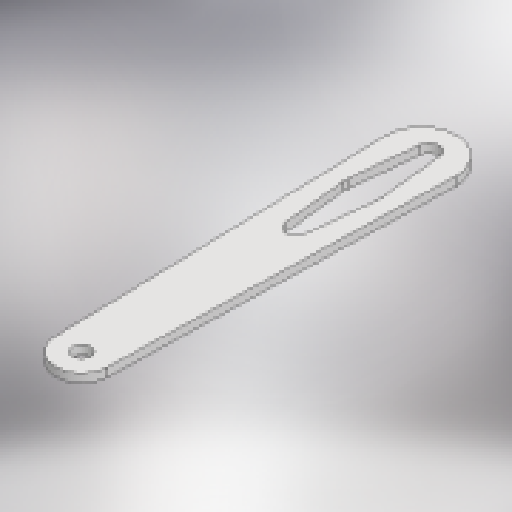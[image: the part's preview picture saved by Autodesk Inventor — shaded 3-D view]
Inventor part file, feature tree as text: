
AUTODESK INVENTOR PART (.ipt)
format: ipt  version: 2024 (Build 280153000, 153)  size: 201,216 bytes
history: native  units: in
note: dims shown in document units (in); Inventor stores cm internally (conversion verified against a paired STEP export)
features: extrude x2, sketch x2, projected_geometry x1
ambient origin geometry x8: Origin, YZ Plane, XZ Plane, XY Plane, X Axis, Y Axis, Z Axis, Center Point
bodies: Solid1 (feature_tree)
feature tree (5):
  extrude  "Extrusion1"  Depth=0.0625in
  extrude  "Extrusion2"  Depth=0.0625in
  sketch  "Sketch1"  dims[d2=0.0625in d3=0.0in d4=0.2165in]
  sketch  "Sketch2"  dims[d5=0.1181in d6=0.1181in d7=0.9449in d8=0.2165in d9=0.0118in d13=2.0in d15=0.125in d17=0.125in d19=0.25in d20=0.25in d21=0.0625in d22=0.0in]
  projected_geometry  "Projected Loop1"
